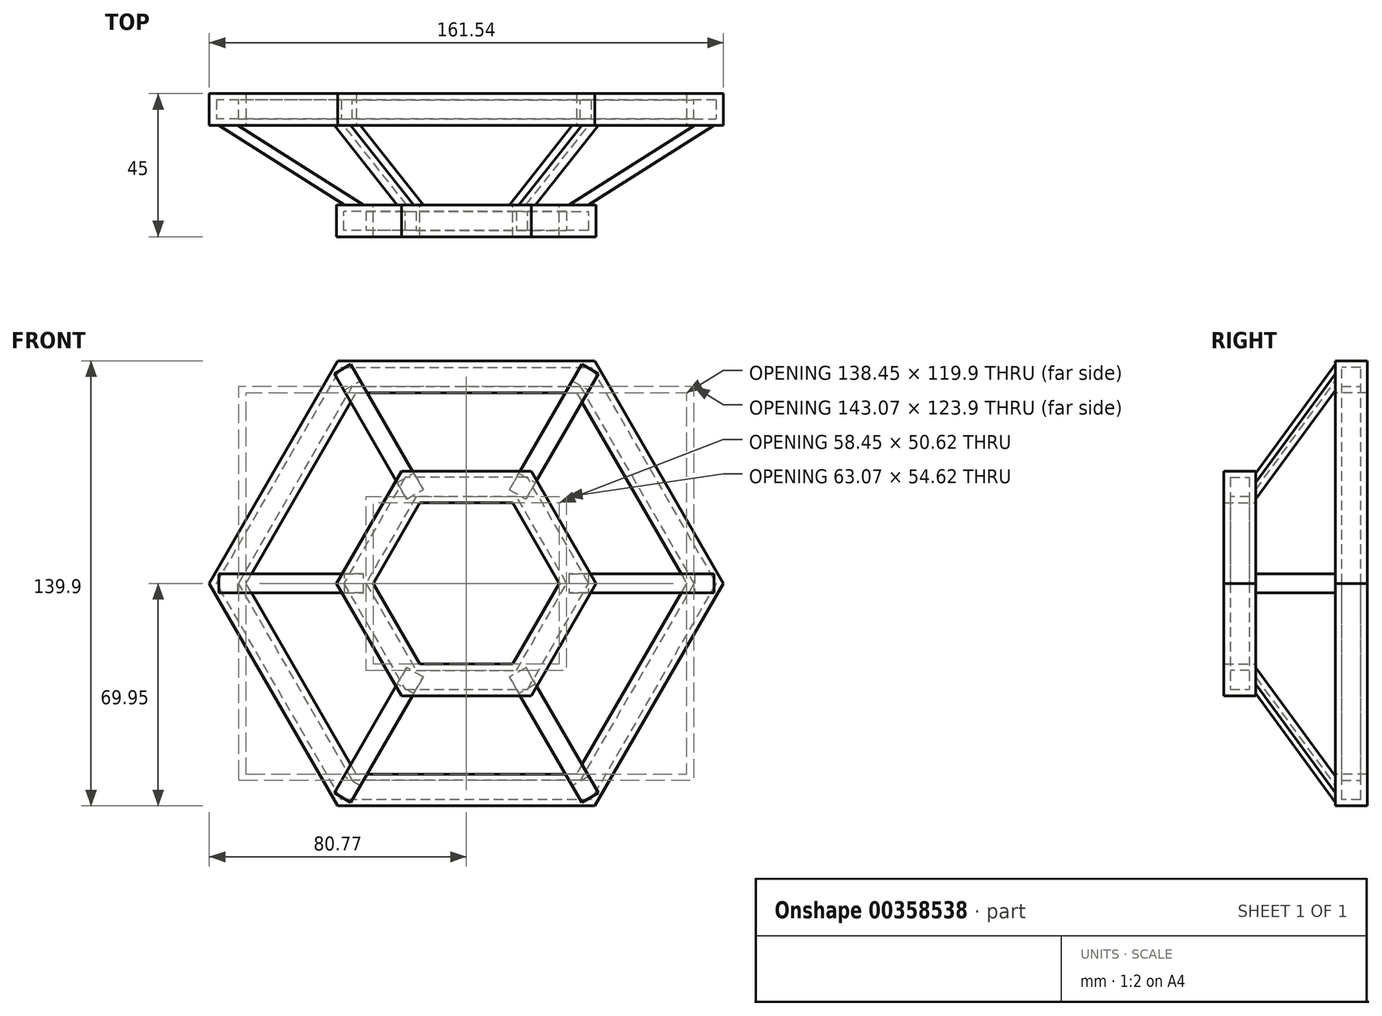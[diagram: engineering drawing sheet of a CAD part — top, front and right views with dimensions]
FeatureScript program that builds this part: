
annotation { "Feature Type Name" : "Feature", "Feature Type Description" : "" }
export const myFeature = defineFeature(function(context is Context, id is Id, definition is map)
    precondition{}
    {
        {
            var Q0;
            Q0=qCreatedBy(makeId("Front.planeOp"),FACE);
            var sketch = newSketch(context, id + "F0", { "sketchPlane" : qUnion([Q0])});
            skCircle(sketch, "E0.cCircle", {"center": v(0, 0) * mm, "radius": 64.95 * mm, "construction": true});
            skLineSegment(sketch, "E0.0", {"start": v(-37.5, 64.95) * mm, "end": v(37.5, 64.95) * mm});
            skLineSegment(sketch, "E0.1", {"start": v(37.5, 64.95) * mm, "end": v(75, 0) * mm});
            skLineSegment(sketch, "E0.2", {"start": v(75, 0) * mm, "end": v(37.5, -64.95) * mm});
            skLineSegment(sketch, "E0.3", {"start": v(37.5, -64.95) * mm, "end": v(-37.5, -64.95) * mm});
            skLineSegment(sketch, "E0.4", {"start": v(-37.5, -64.95) * mm, "end": v(-75, 0) * mm});
            skLineSegment(sketch, "E0.5", {"start": v(-75, 0) * mm, "end": v(-37.5, 64.95) * mm});
            skPoint(sketch, "E0.0.midPoint", {"position": v(0, 64.95) * mm});
            skSolve(sketch);
        }
        {
            var Q0;
            Q0=qCreatedBy(makeId("Right.planeOp"),FACE);
            var sketch = newSketch(context, id + "F1", { "sketchPlane" : qUnion([Q0])});
            skLineSegment(sketch, "E1.bottom", {"start": v(5, 59.95) * mm, "end": v(-5, 59.95) * mm});
            skLineSegment(sketch, "E1.top", {"start": v(5, 69.95) * mm, "end": v(-5, 69.95) * mm});
            skLineSegment(sketch, "E1.left", {"start": v(5, 59.95) * mm, "end": v(5, 69.95) * mm});
            skLineSegment(sketch, "E1.right", {"start": v(-5, 59.95) * mm, "end": v(-5, 69.95) * mm});
            skPoint(sketch, "E1.middle", {"position": v(0, 64.95) * mm});
            skLineSegment(sketch, "E2.bottom", {"start": v(3, 61.95) * mm, "end": v(-3, 61.95) * mm});
            skLineSegment(sketch, "E2.top", {"start": v(3, 67.95) * mm, "end": v(-3, 67.95) * mm});
            skLineSegment(sketch, "E2.left", {"start": v(3, 61.95) * mm, "end": v(3, 67.95) * mm});
            skLineSegment(sketch, "E2.right", {"start": v(-3, 61.95) * mm, "end": v(-3, 67.95) * mm});
            skSolve(sketch);
        }
        {
            var Q0;
            Q0=makeQuery(id+"F1.imprint","IMPRINT",FACE,{"disambiguationData":[TD([[makeQuery(id+"F1.imprint","IMPRINT",EDGE,{"derivedFrom":sQuery(id+"F1.wireOp",EDGE,"E1.bottom")}),-1.0]])]});
            var Q1;
            Q1=sQuery(id+"F0.wireOp",EDGE,"E0.0");
            var Q2;
            Q2=sQuery(id+"F0.wireOp",EDGE,"E0.5");
            var Q3;
            Q3=sQuery(id+"F0.wireOp",EDGE,"E0.4");
            var Q4;
            Q4=sQuery(id+"F0.wireOp",EDGE,"E0.3");
            var Q5;
            Q5=sQuery(id+"F0.wireOp",EDGE,"E0.2");
            var Q6;
            Q6=sQuery(id+"F0.wireOp",EDGE,"E0.1");
            sweep(context, id + "F2", {"profiles" : qUnion([Q0]), "path" : qUnion([Q1, Q2, Q3, Q4, Q5, Q6])});
        }
        {
            var Q0;
            Q0=qCreatedBy(makeId("Front.planeOp"),FACE);
            cPlane(context, id + "F3", {"entities" : qUnion([Q0]), "cplaneType" : CPlaneType.OFFSET, "offset" : 35 * mm, "width" : 150 * mm, "height" : 150 * mm});
        }
        {
            var Q0;
            Q0=qCreatedBy(id+"F3.planeOp",FACE);
            var sketch = newSketch(context, id + "F4", { "sketchPlane" : qUnion([Q0])});
            skCircle(sketch, "E3.cCircle", {"center": v(0, 0) * mm, "radius": 30.31 * mm, "construction": true});
            skLineSegment(sketch, "E3.0", {"start": v(17.5, -30.31) * mm, "end": v(-17.5, -30.31) * mm});
            skLineSegment(sketch, "E3.1", {"start": v(-17.5, -30.31) * mm, "end": v(-35, 0) * mm});
            skLineSegment(sketch, "E3.2", {"start": v(-35, 0) * mm, "end": v(-17.5, 30.31) * mm});
            skLineSegment(sketch, "E3.3", {"start": v(-17.5, 30.31) * mm, "end": v(17.5, 30.31) * mm});
            skLineSegment(sketch, "E3.4", {"start": v(17.5, 30.31) * mm, "end": v(35, 0) * mm});
            skLineSegment(sketch, "E3.5", {"start": v(35, 0) * mm, "end": v(17.5, -30.31) * mm});
            skPoint(sketch, "E3.0.midPoint", {"position": v(0, -30.31) * mm});
            skSolve(sketch);
        }
        {
            var Q0;
            Q0=qCreatedBy(makeId("Right.planeOp"),FACE);
            var sketch = newSketch(context, id + "F5", { "sketchPlane" : qUnion([Q0])});
            skLineSegment(sketch, "E4.bottom", {"start": v(-40, -25.31) * mm, "end": v(-30, -25.31) * mm});
            skLineSegment(sketch, "E4.top", {"start": v(-40, -35.31) * mm, "end": v(-30, -35.31) * mm});
            skLineSegment(sketch, "E4.left", {"start": v(-40, -25.31) * mm, "end": v(-40, -35.31) * mm});
            skLineSegment(sketch, "E4.right", {"start": v(-30, -25.31) * mm, "end": v(-30, -35.31) * mm});
            skPoint(sketch, "E4.middle", {"position": v(-35, -30.31) * mm});
            skLineSegment(sketch, "E5.bottom", {"start": v(-38, -27.31) * mm, "end": v(-32, -27.31) * mm});
            skLineSegment(sketch, "E5.top", {"start": v(-38, -33.31) * mm, "end": v(-32, -33.31) * mm});
            skLineSegment(sketch, "E5.left", {"start": v(-38, -27.31) * mm, "end": v(-38, -33.31) * mm});
            skLineSegment(sketch, "E5.right", {"start": v(-32, -27.31) * mm, "end": v(-32, -33.31) * mm});
            skSolve(sketch);
        }
        {
            var Q0;
            Q0=makeQuery(id+"F5.imprint","IMPRINT",FACE,{"disambiguationData":[TD([[makeQuery(id+"F5.imprint","IMPRINT",EDGE,{"derivedFrom":sQuery(id+"F5.wireOp",EDGE,"E4.bottom")}),-1.0]])]});
            var Q1;
            Q1=sQuery(id+"F4.wireOp",EDGE,"E3.0");
            var Q2;
            Q2=sQuery(id+"F4.wireOp",EDGE,"E3.1");
            var Q3;
            Q3=sQuery(id+"F4.wireOp",EDGE,"E3.2");
            var Q4;
            Q4=sQuery(id+"F4.wireOp",EDGE,"E3.3");
            var Q5;
            Q5=sQuery(id+"F4.wireOp",EDGE,"E3.4");
            var Q6;
            Q6=sQuery(id+"F4.wireOp",EDGE,"E3.5");
            sweep(context, id + "F6", {"profiles" : qUnion([Q0]), "path" : qUnion([Q1, Q2, Q3, Q4, Q5, Q6])});
        }
        {
            var Q0;
            Q0=qCreatedBy(makeId("Top.planeOp"),FACE);
            var sketch = newSketch(context, id + "F7", { "sketchPlane" : qUnion([Q0])});
            skLineSegment(sketch, "E6", {"start": v(32.27, -30) * mm, "end": v(71.77, -5) * mm});
            skLineSegment(sketch, "E7", {"start": v(71.77, -5) * mm, "end": v(77.77, -5) * mm});
            skLineSegment(sketch, "E8", {"start": v(77.77, -5) * mm, "end": v(38.27, -30) * mm});
            skLineSegment(sketch, "E9", {"start": v(38.27, -30) * mm, "end": v(32.27, -30) * mm});
            skSolve(sketch);
        }
        {
            var Q0;
            Q0 = qSketchRegion(id + "F7", true);
            extrude(context, id + "F8", {"entities" : qUnion([Q0]), "endBound" : BoundingType.SYMMETRIC, "depth" : 6 * mm});
        }
        {
            var Q0;
            Q0=qCreatedBy(makeId("Right.planeOp"),FACE);
            var sketch = newSketch(context, id + "F9", { "sketchPlane" : qUnion([Q0])});
            skLineSegment(sketch, "E10", {"start": v(-118.7, 0) * mm, "end": v(86.37, 0) * mm, "construction": true});
            skSolve(sketch);
        }
        {
            var Q0;
            Q0=makeQuery(id+"F8.opExtrude","SWEPT_BODY",BODY,{"disambiguationData":[OSD([sQuery(id+"F7.wireOp",EDGE,"E6"),sQuery(id+"F7.wireOp",EDGE,"E7"),sQuery(id+"F7.wireOp",EDGE,"E8"),sQuery(id+"F7.wireOp",EDGE,"E9")])]});
            var Q1;
            Q1=sQuery(id+"F9.wireOp",EDGE,"E10");
            circularPattern(context, id + "F10", {"entities" : qUnion([Q0]), "axis" : qUnion([Q1]), "angle" : 360 * degree, "instanceCount" : 6, "equalSpace" : true});
        }
    });
